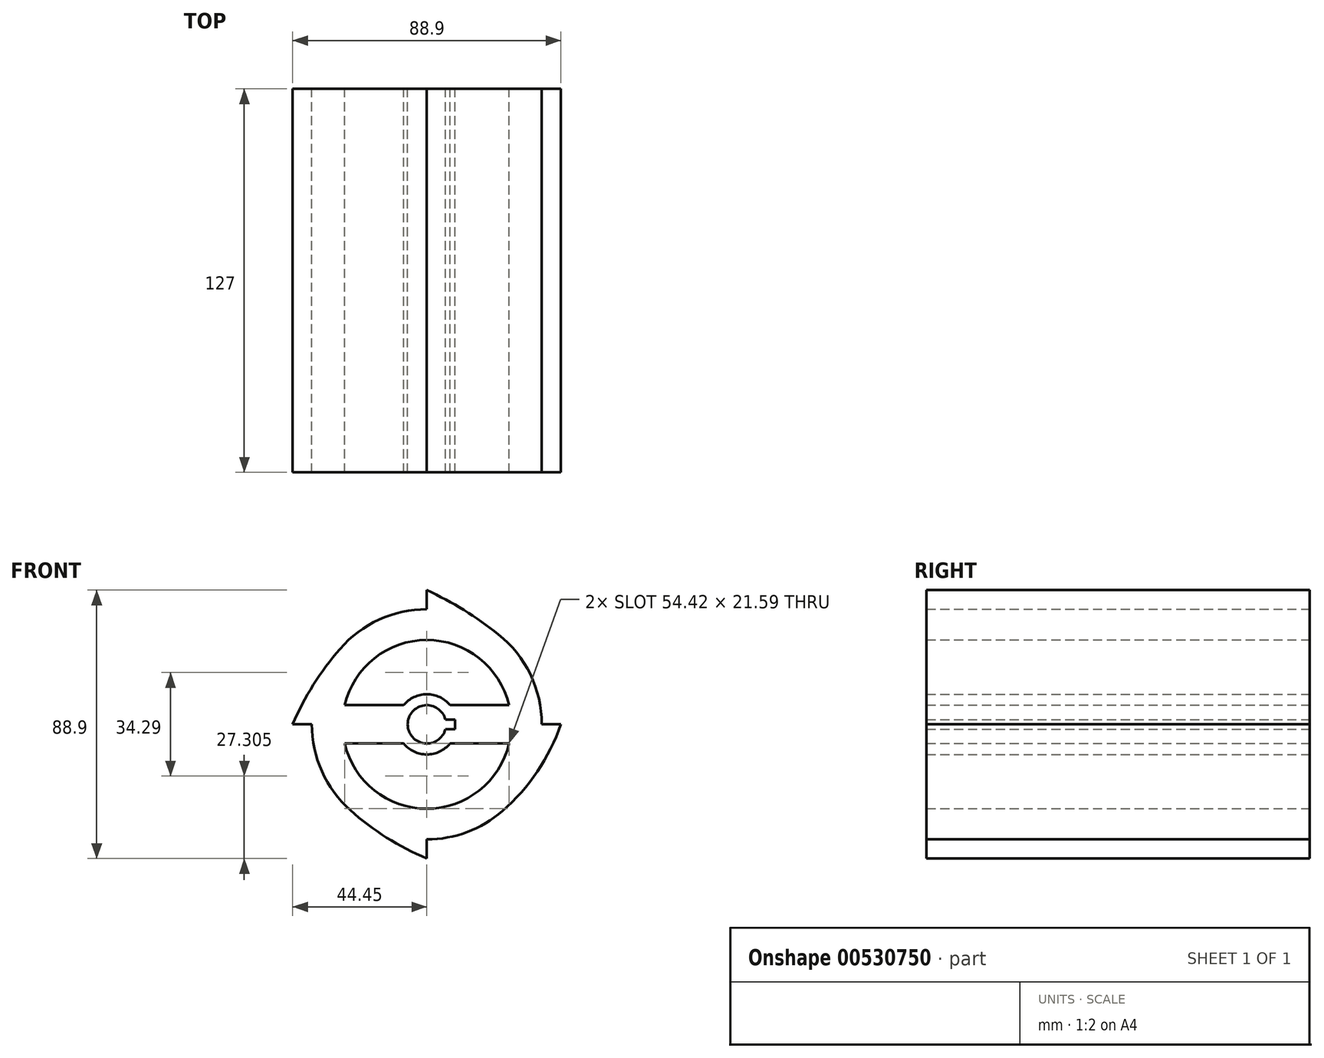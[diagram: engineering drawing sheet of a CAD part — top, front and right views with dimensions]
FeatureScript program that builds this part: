
annotation { "Feature Type Name" : "Feature", "Feature Type Description" : "" }
export const myFeature = defineFeature(function(context is Context, id is Id, definition is map)
    precondition{}
    {
        {
            var Q0;
            Q0=qCreatedBy(makeId("Front.planeOp"),FACE);
            var sketch = newSketch(context, id + "F0", { "sketchPlane" : qUnion([Q0])});
            skCircle(sketch, "E0", {"center": v(0, 0) * mm, "radius": 38.1 * mm});
            skLineSegment(sketch, "E1", {"start": v(-44.45, 0) * mm, "end": v(44.45, 0) * mm});
            skArc(sketch, "E2", {"start": v(23.7, 29.83) * mm, "mid": v(12.29, 37.84) * mm, "end": v(0, 44.45) * mm});
            skArc(sketch, "E3", {"start": v(-28.78, 24.96) * mm, "mid": v(-37.58, 13.09) * mm, "end": v(-44.45, 0) * mm});
            skArc(sketch, "E4", {"start": v(-25.36, -28.44) * mm, "mid": v(-13.34, -37.5) * mm, "end": v(0, -44.45) * mm});
            skArc(sketch, "E5", {"start": v(25.05, -28.7) * mm, "mid": v(36.62, -15.62) * mm, "end": v(44.45, 0) * mm});
            skArc(sketch, "E6", {"start": v(27.2, 6.35) * mm, "mid": v(0, 27.94) * mm, "end": v(-27.2, 6.35) * mm});
            skArc(sketch, "E7", {"start": v(-27.2, -6.35) * mm, "mid": v(0, -27.94) * mm, "end": v(27.2, -6.35) * mm});
            skCircle(sketch, "E8", {"center": v(0, 0) * mm, "radius": 6.35 * mm});
            skLineSegment(sketch, "E9.bottom", {"start": v(-9.4, 1.59) * mm, "end": v(9.4, 1.59) * mm});
            skLineSegment(sketch, "E9.top", {"start": v(-9.4, -1.59) * mm, "end": v(9.4, -1.59) * mm});
            skLineSegment(sketch, "E9.left", {"start": v(-9.4, 1.59) * mm, "end": v(-9.4, -1.59) * mm});
            skLineSegment(sketch, "E9.right", {"start": v(9.4, 1.59) * mm, "end": v(9.4, -1.59) * mm});
            skLineSegment(sketch, "E10", {"start": v(-27.2, -6.35) * mm, "end": v(-7.7, -6.35) * mm});
            skLineSegment(sketch, "E11", {"start": v(-27.2, 6.35) * mm, "end": v(-7.7, 6.35) * mm});
            skLineSegment(sketch, "E12", {"start": v(27.2, -6.35) * mm, "end": v(7.7, -6.35) * mm});
            skLineSegment(sketch, "E13", {"start": v(27.2, 6.35) * mm, "end": v(7.7, 6.35) * mm});
            skCircle(sketch, "E14", {"center": v(0, 0) * mm, "radius": 9.97 * mm});
            skLineSegment(sketch, "E15", {"start": v(0, -44.45) * mm, "end": v(0, -38.1) * mm});
            skLineSegment(sketch, "E16", {"start": v(0, 44.45) * mm, "end": v(0, 38.1) * mm});
            skSolve(sketch);
        }
        {
            var Q0;
            Q0 = qSketchRegion(id + "F0", true);
            var Q1;
            {var subQ5=sQuery(id+"F0.wireOp",EDGE,"E14");var subQ6=sQuery(id+"F0.wireOp",EDGE,"E1");var subQ7=makeQuery(id+"F0.imprint","INTERSECT",VERTEX,{"disambiguationData":[OD(0.0)],"derivedFrom":[subQ6,subQ5]});Q1=makeQuery(id+"F0.imprint","IMPRINT",FACE,{"disambiguationData":[TD([[makeQuery(id+"F0.imprint","IMPRINT",EDGE,{"disambiguationData":[TD([[subQ7,-1.0]])],"derivedFrom":subQ6}),-1.0]])]});}
            var Q2;
            {var subQ6=sQuery(id+"F0.wireOp",EDGE,"E1");var subQ10=sQuery(id+"F0.wireOp",EDGE,"E14");var subQ12=makeQuery(id+"F0.imprint","INTERSECT",VERTEX,{"disambiguationData":[OD(0.0)],"derivedFrom":[subQ6,subQ10]});Q2=makeQuery(id+"F0.imprint","IMPRINT",FACE,{"disambiguationData":[TD([[makeQuery(id+"F0.imprint","IMPRINT",EDGE,{"disambiguationData":[TD([[subQ12,-1.0]])],"derivedFrom":subQ6}),1.0]])]});}
            var Q3;
            {var subQ0=sQuery(id+"F0.wireOp",EDGE,"E9.left");var subQ1=sQuery(id+"F0.wireOp",EDGE,"E1");var subQ2=makeQuery(id+"F0.imprint","INTERSECT",VERTEX,{"derivedFrom":[subQ1,subQ0]});Q3=makeQuery(id+"F0.imprint","IMPRINT",FACE,{"disambiguationData":[TD([[makeQuery(id+"F0.imprint","IMPRINT",EDGE,{"disambiguationData":[TD([[subQ2,-1.0]])],"derivedFrom":subQ1}),1.0]])]});}
            var Q4;
            {var subQ0=sQuery(id+"F0.wireOp",EDGE,"E9.left");var subQ1=sQuery(id+"F0.wireOp",EDGE,"E1");var subQ2=makeQuery(id+"F0.imprint","INTERSECT",VERTEX,{"derivedFrom":[subQ1,subQ0]});Q4=makeQuery(id+"F0.imprint","IMPRINT",FACE,{"disambiguationData":[TD([[makeQuery(id+"F0.imprint","IMPRINT",EDGE,{"disambiguationData":[TD([[subQ2,-1.0]])],"derivedFrom":subQ1}),-1.0]])]});}
            extrude(context, id + "F1", {"entities" : qUnion([Q0, Q1, Q2, Q3, Q4]), "depth" : 127 * mm, "offsetDistance" : 25.4 * mm});
        }
    });
